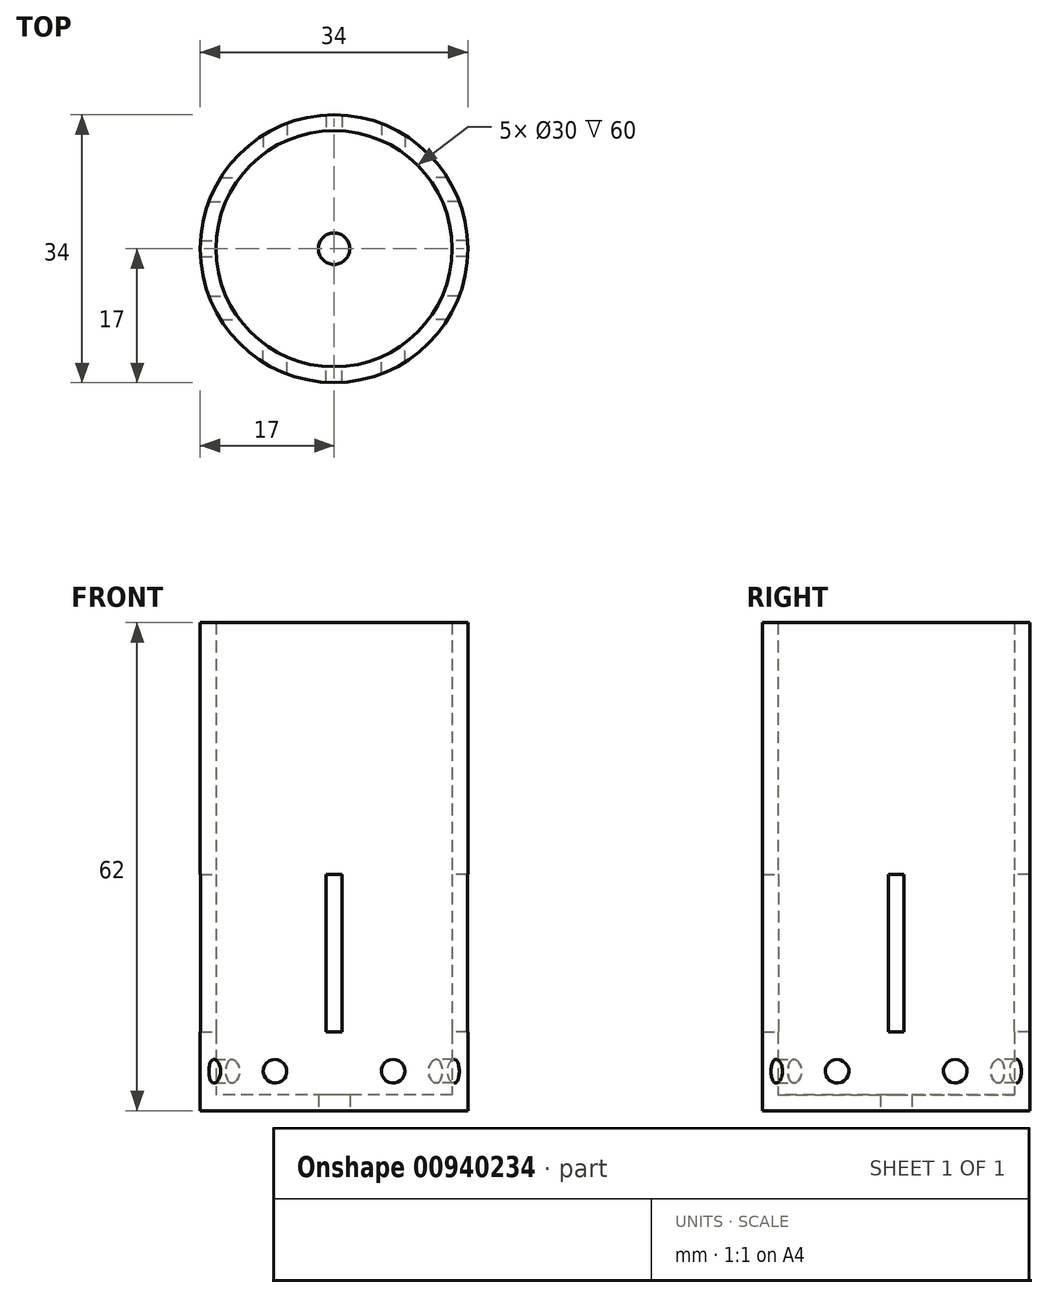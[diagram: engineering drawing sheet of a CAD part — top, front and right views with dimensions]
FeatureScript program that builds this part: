
annotation { "Feature Type Name" : "Feature", "Feature Type Description" : "" }
export const myFeature = defineFeature(function(context is Context, id is Id, definition is map)
    precondition{}
    {
        {
            var Q0;
            Q0=qCreatedBy(makeId("Top.planeOp"),FACE);
            var sketch = newSketch(context, id + "F0", { "sketchPlane" : qUnion([Q0])});
            skCircle(sketch, "E0", {"center": v(0, 0) * mm, "radius": 17 * mm});
            skSolve(sketch);
        }
        {
            var Q0;
            Q0 = qSketchRegion(id + "F0", true);
            extrude(context, id + "F1", {"entities" : qUnion([Q0]), "depth" : 62 * mm, "offsetDistance" : 25 * mm});
        }
        {
            var Q0;
            Q0=makeQuery(id+"F1.opExtrude","CAP_FACE",FACE,{"disambiguationData":[OSD([sQuery(id+"F0.wireOp",EDGE,"E0")])],"isStart":false});
            shell(context, id + "F2", {"entities" : qUnion([Q0]), "thickness" : 2 * mm});
        }
        {
            var Q0;
            Q0=qCreatedBy(makeId("Front.planeOp"),FACE);
            var sketch = newSketch(context, id + "F3", { "sketchPlane" : qUnion([Q0])});
            skLineSegment(sketch, "E1", {"start": v(0, 0) * mm, "end": v(0, 20) * mm, "construction": true});
            skLineSegment(sketch, "E2.bottom", {"start": v(-1, 10) * mm, "end": v(1, 10) * mm});
            skLineSegment(sketch, "E2.top", {"start": v(-1, 30) * mm, "end": v(1, 30) * mm});
            skLineSegment(sketch, "E2.left", {"start": v(-1, 10) * mm, "end": v(-1, 30) * mm});
            skLineSegment(sketch, "E2.right", {"start": v(1, 10) * mm, "end": v(1, 30) * mm});
            skPoint(sketch, "E2.middle", {"position": v(0, 20) * mm});
            skPoint(sketch, "E2.cornerSnap0", {"position": v(0, 10) * mm});
            skSolve(sketch);
        }
        {
            var Q0;
            Q0 = qSketchRegion(id + "F3", true);
            extrude(context, id + "F4", {"entities" : qUnion([Q0]), "operationType" : NewBodyOperationType.REMOVE, "oppositeDirection" : true, "depth" : 25 * mm, "offsetDistance" : 25 * mm});
        }
        {
            var Q0;
            Q0=qCreatedBy(makeId("Front.planeOp"),FACE);
            var sketch = newSketch(context, id + "F5", { "sketchPlane" : qUnion([Q0])});
            skLineSegment(sketch, "E3", {"start": v(0, 0) * mm, "end": v(0, 20) * mm, "construction": true});
            skLineSegment(sketch, "E4.bottom", {"start": v(-1, 10) * mm, "end": v(1, 10) * mm});
            skLineSegment(sketch, "E4.top", {"start": v(-1, 30) * mm, "end": v(1, 30) * mm});
            skLineSegment(sketch, "E4.left", {"start": v(-1, 10) * mm, "end": v(-1, 30) * mm});
            skLineSegment(sketch, "E4.right", {"start": v(1, 10) * mm, "end": v(1, 30) * mm});
            skPoint(sketch, "E4.middle", {"position": v(0, 20) * mm});
            skPoint(sketch, "E4.cornerSnap0", {"position": v(0, 10) * mm});
            skSolve(sketch);
        }
        {
            var Q0;
            Q0 = qSketchRegion(id + "F5", true);
            extrude(context, id + "F6", {"entities" : qUnion([Q0]), "operationType" : NewBodyOperationType.REMOVE, "depth" : 25 * mm, "offsetDistance" : 25 * mm});
        }
        {
            var Q0;
            Q0=qCreatedBy(makeId("Right.planeOp"),FACE);
            var sketch = newSketch(context, id + "F7", { "sketchPlane" : qUnion([Q0])});
            skLineSegment(sketch, "E5", {"start": v(0, 0) * mm, "end": v(0, 20) * mm, "construction": true});
            skLineSegment(sketch, "E6.bottom", {"start": v(-1, 10) * mm, "end": v(1, 10) * mm});
            skLineSegment(sketch, "E6.top", {"start": v(-1, 30) * mm, "end": v(1, 30) * mm});
            skLineSegment(sketch, "E6.left", {"start": v(-1, 10) * mm, "end": v(-1, 30) * mm});
            skLineSegment(sketch, "E6.right", {"start": v(1, 10) * mm, "end": v(1, 30) * mm});
            skPoint(sketch, "E6.middle", {"position": v(0, 20) * mm});
            skPoint(sketch, "E6.cornerSnap0", {"position": v(0, 10) * mm});
            skSolve(sketch);
        }
        {
            var Q0;
            Q0 = qSketchRegion(id + "F7", true);
            extrude(context, id + "F8", {"entities" : qUnion([Q0]), "operationType" : NewBodyOperationType.REMOVE, "oppositeDirection" : true, "depth" : 25 * mm, "offsetDistance" : 25 * mm});
        }
        {
            var Q0;
            Q0=qCreatedBy(makeId("Right.planeOp"),FACE);
            var sketch = newSketch(context, id + "F9", { "sketchPlane" : qUnion([Q0])});
            skLineSegment(sketch, "E7", {"start": v(0, 0) * mm, "end": v(0, 20) * mm, "construction": true});
            skLineSegment(sketch, "E8.bottom", {"start": v(-1, 10) * mm, "end": v(1, 10) * mm});
            skLineSegment(sketch, "E8.top", {"start": v(-1, 30) * mm, "end": v(1, 30) * mm});
            skLineSegment(sketch, "E8.left", {"start": v(-1, 10) * mm, "end": v(-1, 30) * mm});
            skLineSegment(sketch, "E8.right", {"start": v(1, 10) * mm, "end": v(1, 30) * mm});
            skPoint(sketch, "E8.middle", {"position": v(0, 20) * mm});
            skPoint(sketch, "E8.cornerSnap0", {"position": v(0, 10) * mm});
            skSolve(sketch);
        }
        {
            var Q0;
            Q0 = qSketchRegion(id + "F9", true);
            extrude(context, id + "F10", {"entities" : qUnion([Q0]), "operationType" : NewBodyOperationType.REMOVE, "depth" : 25 * mm, "offsetDistance" : 25 * mm});
        }
        {
            var Q0;
            Q0=qCreatedBy(makeId("Front.planeOp"),FACE);
            var sketch = newSketch(context, id + "F11", { "sketchPlane" : qUnion([Q0])});
            skLineSegment(sketch, "E9", {"start": v(0, 0) * mm, "end": v(7.5, 0) * mm, "construction": true});
            skLineSegment(sketch, "E10", {"start": v(7.5, 0) * mm, "end": v(7.5, 5) * mm, "construction": true});
            skCircle(sketch, "E11", {"center": v(7.5, 5) * mm, "radius": 1.5 * mm});
            skLineSegment(sketch, "E12", {"start": v(0, 62.21) * mm, "end": v(0, 0) * mm, "construction": true});
            skCircle(sketch, "E13.MirrorC", {"center": v(-7.5, 5) * mm, "radius": 1.5 * mm});
            skSolve(sketch);
        }
        {
            var Q0;
            Q0 = qSketchRegion(id + "F11", true);
            extrude(context, id + "F12", {"entities" : qUnion([Q0]), "operationType" : NewBodyOperationType.REMOVE, "oppositeDirection" : true, "depth" : 25 * mm, "offsetDistance" : 25 * mm});
        }
        {
            var Q0;
            Q0=qCreatedBy(makeId("Front.planeOp"),FACE);
            var sketch = newSketch(context, id + "F13", { "sketchPlane" : qUnion([Q0])});
            skLineSegment(sketch, "E14", {"start": v(0, 0) * mm, "end": v(7.5, 0) * mm, "construction": true});
            skLineSegment(sketch, "E15", {"start": v(7.5, 0) * mm, "end": v(7.5, 5) * mm, "construction": true});
            skCircle(sketch, "E16", {"center": v(7.5, 5) * mm, "radius": 1.5 * mm});
            skLineSegment(sketch, "E17", {"start": v(0, 62.93) * mm, "end": v(0, 0) * mm, "construction": true});
            skCircle(sketch, "E18.MirrorC", {"center": v(-7.5, 5) * mm, "radius": 1.5 * mm});
            skSolve(sketch);
        }
        {
            var Q0;
            Q0 = qSketchRegion(id + "F13", true);
            extrude(context, id + "F14", {"entities" : qUnion([Q0]), "operationType" : NewBodyOperationType.REMOVE, "depth" : 25 * mm, "offsetDistance" : 25 * mm});
        }
        {
            var Q0;
            Q0=qCreatedBy(makeId("Right.planeOp"),FACE);
            var sketch = newSketch(context, id + "F15", { "sketchPlane" : qUnion([Q0])});
            skLineSegment(sketch, "E19", {"start": v(0, 0) * mm, "end": v(7.5, 0) * mm});
            skLineSegment(sketch, "E20", {"start": v(7.5, 0) * mm, "end": v(7.5, 5) * mm});
            skCircle(sketch, "E21", {"center": v(7.5, 5) * mm, "radius": 1.5 * mm});
            skLineSegment(sketch, "E22", {"start": v(0, 61.98) * mm, "end": v(0, 0) * mm, "construction": true});
            skCircle(sketch, "E23.MirrorC", {"center": v(-7.5, 5) * mm, "radius": 1.5 * mm});
            skSolve(sketch);
        }
        {
            var Q0;
            Q0 = qSketchRegion(id + "F15", true);
            extrude(context, id + "F16", {"entities" : qUnion([Q0]), "operationType" : NewBodyOperationType.REMOVE, "oppositeDirection" : true, "depth" : 25 * mm, "offsetDistance" : 25 * mm});
        }
        {
            var Q0;
            Q0=qCreatedBy(makeId("Right.planeOp"),FACE);
            var sketch = newSketch(context, id + "F17", { "sketchPlane" : qUnion([Q0])});
            skLineSegment(sketch, "E24", {"start": v(0, 0) * mm, "end": v(-7.5, 0) * mm, "construction": true});
            skLineSegment(sketch, "E25", {"start": v(-7.5, 0) * mm, "end": v(-7.5, 5) * mm, "construction": true});
            skLineSegment(sketch, "E26", {"start": v(0, 62) * mm, "end": v(0, 0) * mm, "construction": true});
            skCircle(sketch, "E27", {"center": v(-7.5, 5) * mm, "radius": 1.5 * mm});
            skCircle(sketch, "E28.MirrorC", {"center": v(7.5, 5) * mm, "radius": 1.5 * mm});
            skSolve(sketch);
        }
        {
            var Q0;
            Q0 = qSketchRegion(id + "F17", true);
            extrude(context, id + "F18", {"entities" : qUnion([Q0]), "operationType" : NewBodyOperationType.REMOVE, "depth" : 25 * mm, "offsetDistance" : 25 * mm});
        }
        {
            var Q0;
            Q0=makeQuery(id+"F1.opExtrude","CAP_FACE",FACE,{"disambiguationData":[OSD([sQuery(id+"F0.wireOp",EDGE,"E0")])],"isStart":true});
            var sketch = newSketch(context, id + "F19", { "sketchPlane" : qUnion([Q0])});
            skCircle(sketch, "E29", {"center": v(0, 0) * mm, "radius": 2 * mm});
            skSolve(sketch);
        }
        {
            var Q0;
            Q0 = qSketchRegion(id + "F19", true);
            extrude(context, id + "F20", {"entities" : qUnion([Q0]), "operationType" : NewBodyOperationType.REMOVE, "oppositeDirection" : true, "depth" : 25 * mm, "offsetDistance" : 25 * mm});
        }
    });
